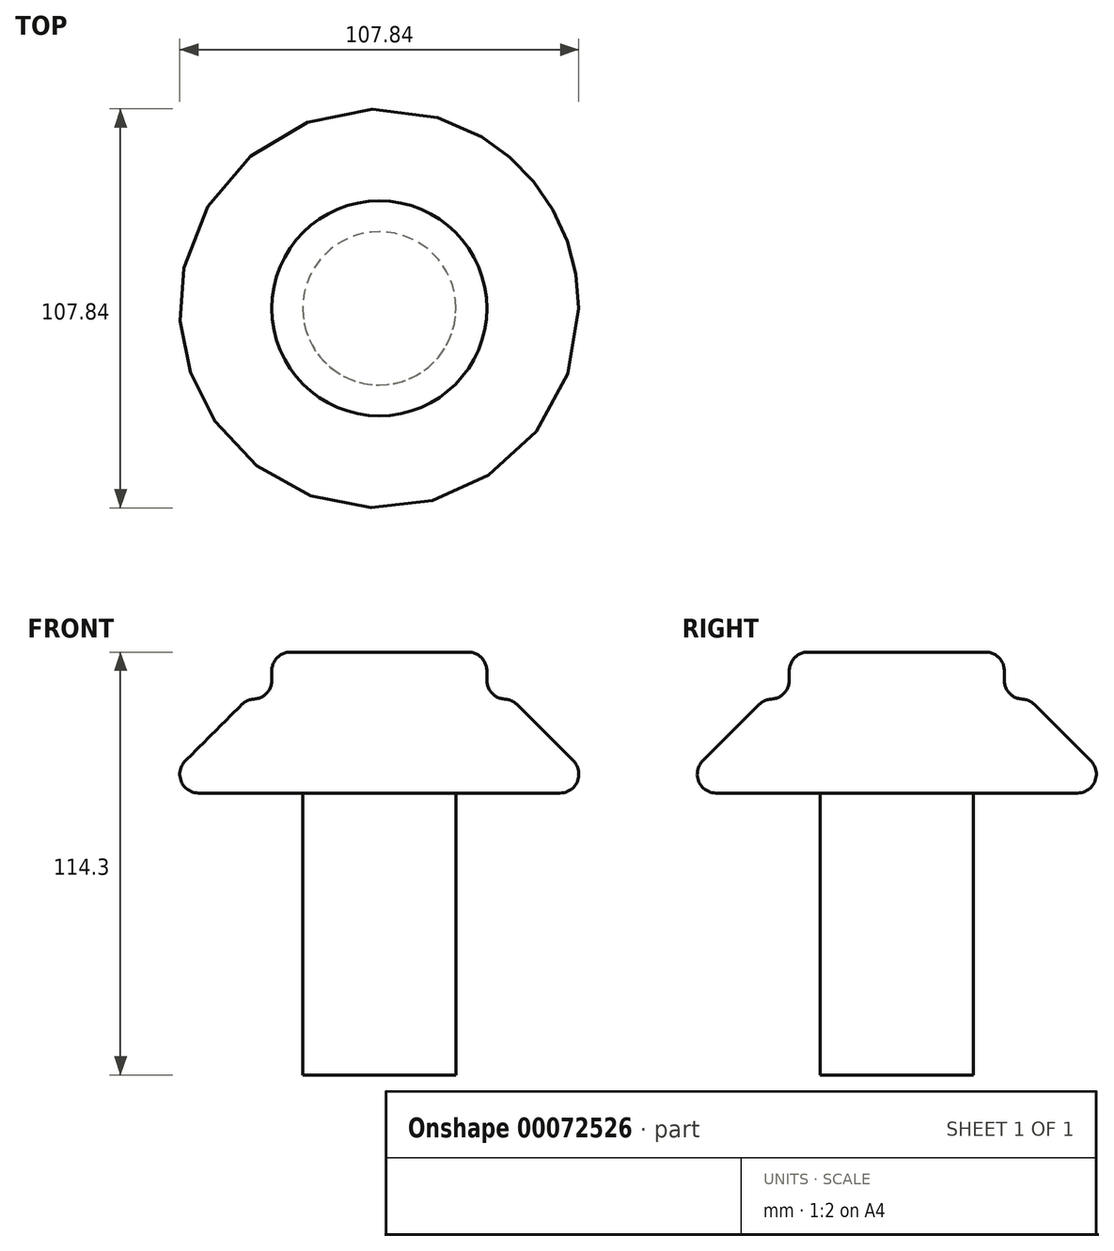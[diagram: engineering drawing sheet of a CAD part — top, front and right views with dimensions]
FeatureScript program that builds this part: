
annotation { "Feature Type Name" : "Feature", "Feature Type Description" : "" }
export const myFeature = defineFeature(function(context is Context, id is Id, definition is map)
    precondition{}
    {
        {
            var Q0;
            Q0=qCreatedBy(makeId("Top.planeOp"),FACE);
            var sketch = newSketch(context, id + "F0", { "sketchPlane" : qUnion([Q0])});
            skCircle(sketch, "E0", {"center": v(0, 0) * mm, "radius": 61.1 * mm});
            skSolve(sketch);
        }
        {
            var Q0;
            Q0=makeQuery(id+"F0.imprint","IMPRINT",FACE,{"disambiguationData":[TD([[makeQuery(id+"F0.imprint","IMPRINT",EDGE,{"derivedFrom":sQuery(id+"F0.wireOp",EDGE,"E0")}),1.0]])]});
            extrude(context, id + "F1", {"entities" : qUnion([Q0]), "depth" : 25.4 * mm});
        }
        {
            var Q0;
            Q0=makeQuery(id+"F1.opExtrude","CAP_FACE",FACE,{"disambiguationData":[OSD([sQuery(id+"F0.wireOp",EDGE,"E0")])],"isStart":false});
            var sketch = newSketch(context, id + "F2", { "sketchPlane" : qUnion([Q0])});
            skCircle(sketch, "E1", {"center": v(0, 0) * mm, "radius": 29.06 * mm});
            skSolve(sketch);
        }
        {
            var Q0;
            Q0 = qSketchRegion(id + "F2", true);
            extrude(context, id + "F3", {"entities" : qUnion([Q0]), "operationType" : NewBodyOperationType.ADD, "depth" : 12.7 * mm});
        }
        {
            var Q0;
            Q0=makeQuery(id+"F1.opExtrude","CAP_EDGE",EDGE,{"disambiguationData":[OSD([sQuery(id+"F0.wireOp",EDGE,"E0")])],"isStart":false});
            chamfer(context, id + "F4", {"entities" : qUnion([Q0]), "width" : 25.4 * mm, "tangentPropagation" : true});
        }
        {
            var Q0;
            Q0=makeQuery(id+"F4.opChamfer","BLEND_FACE",FACE,{"disambiguationData":[OSD([sQuery(id+"F0.wireOp",EDGE,"E0")])]});
            var Q1;
            Q1=makeQuery(id+"F3.opExtrude","CAP_EDGE",EDGE,{"disambiguationData":[OSD([sQuery(id+"F2.wireOp",EDGE,"E1")])],"isStart":false});
            fillet(context, id + "F5", {"entities" : qUnion([Q0, Q1]), "radius" : 5.08 * mm, "tangentPropagation" : true, "allowEdgeOverflow" : false});
        }
        {
            var Q0;
            Q0=makeQuery(id+"F3.opExtrude","SWEPT_FACE",FACE,{"disambiguationData":[OSD([sQuery(id+"F2.wireOp",EDGE,"E1")])]});
            fillet(context, id + "F6", {"entities" : qUnion([Q0]), "radius" : 5.08 * mm, "tangentPropagation" : true, "allowEdgeOverflow" : false});
        }
        {
            var Q0;
            Q0=qCreatedBy(makeId("Top.planeOp"),FACE);
            var sketch = newSketch(context, id + "F7", { "sketchPlane" : qUnion([Q0])});
            skCircle(sketch, "E2", {"center": v(-0.96, -1.88) * mm, "radius": 17.22 * mm});
            skSolve(sketch);
        }
        {
            var Q0;
            Q0=makeQuery(id+"F7.imprint","IMPRINT",FACE,{"disambiguationData":[TD([[makeQuery(id+"F7.imprint","IMPRINT",EDGE,{"derivedFrom":sQuery(id+"F7.wireOp",EDGE,"E2")}),1.0]])]});
            extrude(context, id + "F8", {"entities" : qUnion([Q0]), "operationType" : NewBodyOperationType.ADD, "depth" : 25.4 * mm});
        }
        {
            var Q0;
            Q0=makeQuery(id+"F1.opExtrude","CAP_FACE",FACE,{"disambiguationData":[OSD([sQuery(id+"F0.wireOp",EDGE,"E0")])],"isStart":true});
            var sketch = newSketch(context, id + "F9", { "sketchPlane" : qUnion([Q0])});
            skCircle(sketch, "E3", {"center": v(0, 0) * mm, "radius": 20.7 * mm});
            skSolve(sketch);
        }
        {
            var Q0;
            Q0=makeQuery(id+"F9.imprint","IMPRINT",FACE,{"disambiguationData":[TD([[makeQuery(id+"F9.imprint","IMPRINT",EDGE,{"derivedFrom":sQuery(id+"F9.wireOp",EDGE,"E3")}),1.0]])]});
            extrude(context, id + "F10", {"entities" : qUnion([Q0]), "operationType" : NewBodyOperationType.ADD, "depth" : 76.2 * mm});
        }
    });
